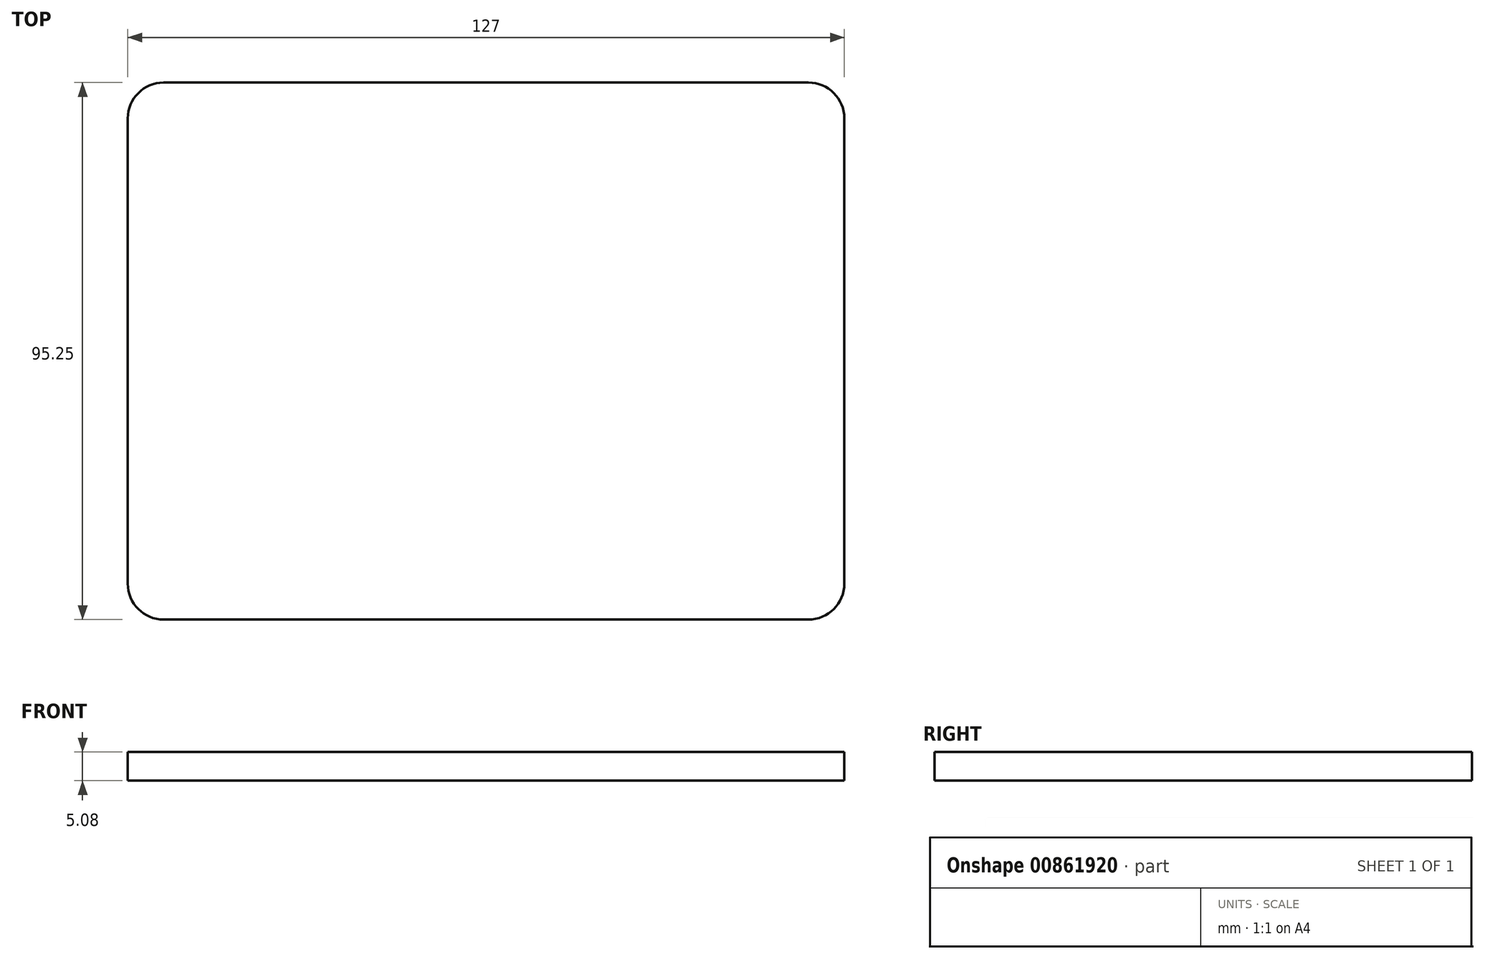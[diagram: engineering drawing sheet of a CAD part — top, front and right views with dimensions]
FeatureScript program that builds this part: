
annotation { "Feature Type Name" : "Feature", "Feature Type Description" : "" }
export const myFeature = defineFeature(function(context is Context, id is Id, definition is map)
    precondition{}
    {
        {
            var Q0;
            Q0=qCreatedBy(makeId("Top.planeOp"),FACE);
            var sketch = newSketch(context, id + "F0", { "sketchPlane" : qUnion([Q0])});
            skLineSegment(sketch, "E0.bottom", {"start": v(-49.84, 69.81) * mm, "end": v(64.46, 69.81) * mm});
            skLineSegment(sketch, "E0.top", {"start": v(-49.84, -25.44) * mm, "end": v(64.46, -25.44) * mm});
            skLineSegment(sketch, "E0.left", {"start": v(-56.2, 63.46) * mm, "end": v(-56.2, -19.09) * mm});
            skLineSegment(sketch, "E0.right", {"start": v(70.8, 63.46) * mm, "end": v(70.8, -19.09) * mm});
            skPoint(sketch, "E1.visualSharp", {"position": v(-56.2, 69.81) * mm});
            skArc(sketch, "E1.filletArc", {"start": v(-49.84, 69.81) * mm, "mid": v(-54.33, 67.95) * mm, "end": v(-56.2, 63.46) * mm});
            skPoint(sketch, "E2.visualSharp", {"position": v(-56.2, -25.44) * mm});
            skArc(sketch, "E2.filletArc", {"start": v(-56.2, -19.09) * mm, "mid": v(-54.33, -23.58) * mm, "end": v(-49.84, -25.44) * mm});
            skPoint(sketch, "E3.visualSharp", {"position": v(70.8, -25.44) * mm});
            skArc(sketch, "E3.filletArc", {"start": v(64.46, -25.44) * mm, "mid": v(68.95, -23.58) * mm, "end": v(70.8, -19.09) * mm});
            skPoint(sketch, "E4.visualSharp", {"position": v(70.8, 69.81) * mm});
            skArc(sketch, "E4.filletArc", {"start": v(70.8, 63.46) * mm, "mid": v(68.95, 67.95) * mm, "end": v(64.46, 69.81) * mm});
            skSolve(sketch);
        }
        {
            var Q0;
            Q0=makeQuery(id+"F0.imprint","IMPRINT",FACE,{"disambiguationData":[TD([[makeQuery(id+"F0.imprint","IMPRINT",EDGE,{"derivedFrom":sQuery(id+"F0.wireOp",EDGE,"E0.bottom")}),-1.0]])]});
            extrude(context, id + "F1", {"entities" : qUnion([Q0]), "depth" : 5.08 * mm, "offsetDistance" : 25.4 * mm});
        }
    });
